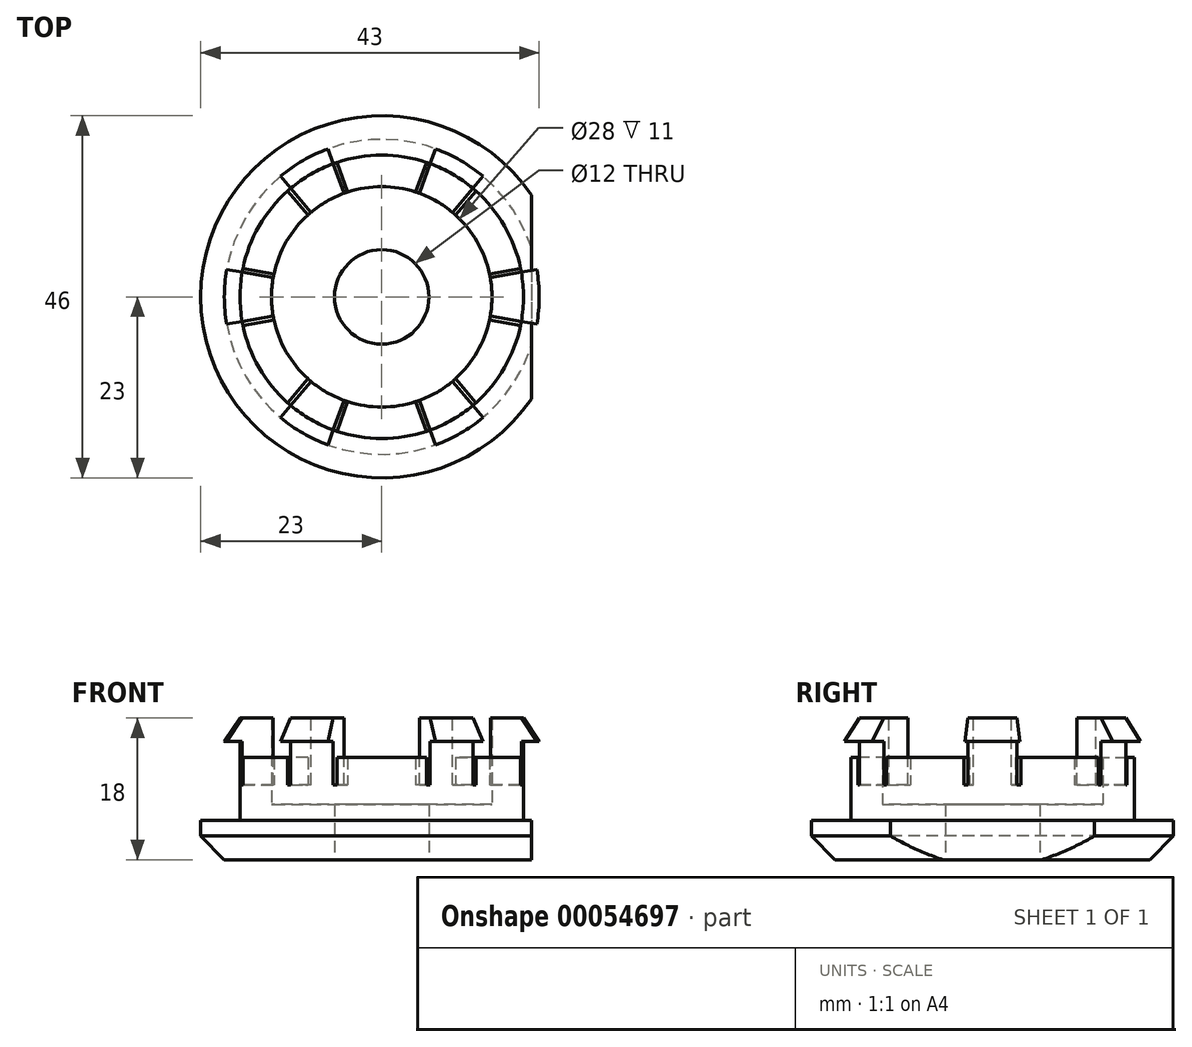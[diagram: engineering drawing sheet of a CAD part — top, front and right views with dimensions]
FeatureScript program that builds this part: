
annotation { "Feature Type Name" : "Feature", "Feature Type Description" : "" }
export const myFeature = defineFeature(function(context is Context, id is Id, definition is map)
    precondition{}
    {
        {
            var Q0;
            Q0=qCreatedBy(makeId("Top.planeOp"),FACE);
            var sketch = newSketch(context, id + "F0", { "sketchPlane" : qUnion([Q0])});
            skCircle(sketch, "E0", {"center": v(0, 0) * mm, "radius": 18 * mm});
            skCircle(sketch, "E1", {"center": v(0, 0) * mm, "radius": 6 * mm});
            skCircle(sketch, "E2", {"center": v(0, 0) * mm, "radius": 23 * mm});
            skCircle(sketch, "E3", {"center": v(0, 0) * mm, "radius": 14 * mm});
            skSolve(sketch);
        }
        {
            var Q0;
            Q0=makeQuery(id+"F0.imprint","IMPRINT",FACE,{"disambiguationData":[TD([[makeQuery(id+"F0.imprint","IMPRINT",EDGE,{"derivedFrom":sQuery(id+"F0.wireOp",EDGE,"E0")}),1.0]])]});
            var Q1;
            Q1=makeQuery(id+"F0.imprint","IMPRINT",FACE,{"disambiguationData":[TD([[makeQuery(id+"F0.imprint","IMPRINT",EDGE,{"derivedFrom":sQuery(id+"F0.wireOp",EDGE,"E1")}),-1.0]])]});
            extrude(context, id + "F1", {"entities" : qUnion([Q0, Q1]), "depth" : 2 * mm});
        }
        {
            var Q0;
            Q0=makeQuery(id+"F0.imprint","IMPRINT",FACE,{"disambiguationData":[TD([[makeQuery(id+"F0.imprint","IMPRINT",EDGE,{"derivedFrom":sQuery(id+"F0.wireOp",EDGE,"E0")}),1.0]])]});
            extrude(context, id + "F2", {"entities" : qUnion([Q0]), "operationType" : NewBodyOperationType.ADD, "depth" : 13 * mm});
        }
        {
            var Q0;
            Q0=makeQuery(id+"F0.imprint","IMPRINT",FACE,{"disambiguationData":[TD([[makeQuery(id+"F0.imprint","IMPRINT",EDGE,{"derivedFrom":sQuery(id+"F0.wireOp",EDGE,"E0")}),-1.0]])]});
            var Q1;
            Q1=makeQuery(id+"F0.imprint","IMPRINT",FACE,{"disambiguationData":[TD([[makeQuery(id+"F0.imprint","IMPRINT",EDGE,{"derivedFrom":sQuery(id+"F0.wireOp",EDGE,"E0")}),1.0]])]});
            var Q2;
            Q2=makeQuery(id+"F0.imprint","IMPRINT",FACE,{"disambiguationData":[TD([[makeQuery(id+"F0.imprint","IMPRINT",EDGE,{"derivedFrom":sQuery(id+"F0.wireOp",EDGE,"E1")}),-1.0]])]});
            extrude(context, id + "F3", {"entities" : qUnion([Q0, Q1, Q2]), "operationType" : NewBodyOperationType.ADD, "oppositeDirection" : true, "depth" : 5 * mm});
        }
        {
            var Q0;
            Q0=makeQuery(id+"F3.opExtrude","CAP_EDGE",EDGE,{"disambiguationData":[OSD([sQuery(id+"F0.wireOp",EDGE,"E2")])],"isStart":false});
            chamfer(context, id + "F4", {"entities" : qUnion([Q0]), "width" : 3 * mm, "tangentPropagation" : true});
        }
        {
            var Q0;
            Q0=qCreatedBy(makeId("Front.planeOp"),FACE);
            var sketch = newSketch(context, id + "F5", { "sketchPlane" : qUnion([Q0])});
            skLineSegment(sketch, "E4", {"start": v(14, 10) * mm, "end": v(14, 13) * mm});
            skLineSegment(sketch, "E5", {"start": v(14, 13) * mm, "end": v(18, 13) * mm});
            skLineSegment(sketch, "E6", {"start": v(18, 13) * mm, "end": v(20, 10) * mm});
            skLineSegment(sketch, "E7", {"start": v(20, 10) * mm, "end": v(14, 10) * mm});
            skLineSegment(sketch, "E8", {"start": v(0, 0) * mm, "end": v(0, 19.84) * mm});
            skLineSegment(sketch, "E9", {"start": v(18, 13) * mm, "end": v(18, 5) * mm});
            skLineSegment(sketch, "E10", {"start": v(18, 5) * mm, "end": v(14, 5) * mm});
            skLineSegment(sketch, "E11", {"start": v(14, 5) * mm, "end": v(14, 10) * mm});
            skSolve(sketch);
        }
        {
            var Q0;
            Q0=makeQuery(id+"F5.imprint","IMPRINT",FACE,{"disambiguationData":[TD([[makeQuery(id+"F5.imprint","IMPRINT",EDGE,{"derivedFrom":sQuery(id+"F5.wireOp",EDGE,"E4")}),-1.0]])]});
            var Q1;
            {var subQ0=sQuery(id+"F5.wireOp",EDGE,"E6");Q1=makeQuery(id+"F5.imprint","IMPRINT",FACE,{"disambiguationData":[TD([[makeQuery(id+"F5.imprint","IMPRINT",EDGE,{"derivedFrom":subQ0}),-1.0]])]});}
            var Q2;
            {var subQ4=sQuery(id+"F5.wireOp",EDGE,"E10");Q2=makeQuery(id+"F5.imprint","IMPRINT",FACE,{"disambiguationData":[TD([[makeQuery(id+"F5.imprint","IMPRINT",EDGE,{"derivedFrom":subQ4}),-1.0]])]});}
            var Q3;
            Q3=sQuery(id+"F5.wireOp",EDGE,"E8");
            revolve(context, id + "F6", {"entities" : qUnion([Q0, Q1, Q2]), "axis" : qUnion([Q3]), "revolveType" : RevolveType.SYMMETRIC, "angle" : 20 * degree});
        }
        {
            var Q0;
            Q0=makeQuery(id+"F6.opRevolve","SWEPT_BODY",BODY,{"disambiguationData":[OSD([sQuery(id+"F5.wireOp",EDGE,"E4"),sQuery(id+"F5.wireOp",EDGE,"E5"),sQuery(id+"F5.wireOp",EDGE,"E6"),sQuery(id+"F5.wireOp",EDGE,"E7")])]});
            var Q1;
            Q1=sQuery(id+"F5.wireOp",EDGE,"E8");
            circularPattern(context, id + "F7", {"entities" : qUnion([Q0]), "axis" : qUnion([Q1]), "angle" : 360 * degree, "instanceCount" : 6, "equalSpace" : true});
        }
        {
            var Q0;
            Q0=makeQuery(id+"F6.opRevolve","SWEPT_BODY",BODY,{"disambiguationData":[OSD([sQuery(id+"F5.wireOp",EDGE,"E4"),sQuery(id+"F5.wireOp",EDGE,"E5"),sQuery(id+"F5.wireOp",EDGE,"E6"),sQuery(id+"F5.wireOp",EDGE,"E7"),sQuery(id+"F5.wireOp",EDGE,"E9"),sQuery(id+"F5.wireOp",EDGE,"E10"),sQuery(id+"F5.wireOp",EDGE,"E11")])]});
            var Q1;
            Q1=makeQuery(id+"F7.opPattern","COPY",BODY,{"derivedFrom":makeQuery(id+"F6.opRevolve","SWEPT_BODY",BODY,{"disambiguationData":[OSD([sQuery(id+"F5.wireOp",EDGE,"E4"),sQuery(id+"F5.wireOp",EDGE,"E5"),sQuery(id+"F5.wireOp",EDGE,"E6"),sQuery(id+"F5.wireOp",EDGE,"E7"),sQuery(id+"F5.wireOp",EDGE,"E9"),sQuery(id+"F5.wireOp",EDGE,"E10"),sQuery(id+"F5.wireOp",EDGE,"E11")])]}),"instanceName":"1"});
            var Q2;
            Q2=makeQuery(id+"F7.opPattern","COPY",BODY,{"derivedFrom":makeQuery(id+"F6.opRevolve","SWEPT_BODY",BODY,{"disambiguationData":[OSD([sQuery(id+"F5.wireOp",EDGE,"E4"),sQuery(id+"F5.wireOp",EDGE,"E5"),sQuery(id+"F5.wireOp",EDGE,"E6"),sQuery(id+"F5.wireOp",EDGE,"E7"),sQuery(id+"F5.wireOp",EDGE,"E9"),sQuery(id+"F5.wireOp",EDGE,"E10"),sQuery(id+"F5.wireOp",EDGE,"E11")])]}),"instanceName":"2"});
            var Q3;
            Q3=makeQuery(id+"F7.opPattern","COPY",BODY,{"derivedFrom":makeQuery(id+"F6.opRevolve","SWEPT_BODY",BODY,{"disambiguationData":[OSD([sQuery(id+"F5.wireOp",EDGE,"E4"),sQuery(id+"F5.wireOp",EDGE,"E5"),sQuery(id+"F5.wireOp",EDGE,"E6"),sQuery(id+"F5.wireOp",EDGE,"E7"),sQuery(id+"F5.wireOp",EDGE,"E9"),sQuery(id+"F5.wireOp",EDGE,"E10"),sQuery(id+"F5.wireOp",EDGE,"E11")])]}),"instanceName":"3"});
            var Q4;
            Q4=makeQuery(id+"F7.opPattern","COPY",BODY,{"derivedFrom":makeQuery(id+"F6.opRevolve","SWEPT_BODY",BODY,{"disambiguationData":[OSD([sQuery(id+"F5.wireOp",EDGE,"E4"),sQuery(id+"F5.wireOp",EDGE,"E5"),sQuery(id+"F5.wireOp",EDGE,"E6"),sQuery(id+"F5.wireOp",EDGE,"E7"),sQuery(id+"F5.wireOp",EDGE,"E9"),sQuery(id+"F5.wireOp",EDGE,"E10"),sQuery(id+"F5.wireOp",EDGE,"E11")])]}),"instanceName":"4"});
            var Q5;
            Q5=makeQuery(id+"F7.opPattern","COPY",BODY,{"derivedFrom":makeQuery(id+"F6.opRevolve","SWEPT_BODY",BODY,{"disambiguationData":[OSD([sQuery(id+"F5.wireOp",EDGE,"E4"),sQuery(id+"F5.wireOp",EDGE,"E5"),sQuery(id+"F5.wireOp",EDGE,"E6"),sQuery(id+"F5.wireOp",EDGE,"E7"),sQuery(id+"F5.wireOp",EDGE,"E9"),sQuery(id+"F5.wireOp",EDGE,"E10"),sQuery(id+"F5.wireOp",EDGE,"E11")])]}),"instanceName":"5"});
            var Q6;
            Q6=makeQuery(id+"F1.opExtrude","SWEPT_BODY",BODY,{"disambiguationData":[OSD([sQuery(id+"F0.wireOp",EDGE,"E0"),sQuery(id+"F0.wireOp",EDGE,"E1")])]});
            booleanBodies(context, id + "F8", {"operationType" : BooleanOperationType.SUBTRACTION, "tools" : qUnion([Q0, Q1, Q2, Q3, Q4, Q5]), "targets" : qUnion([Q6]), "offset" : true, "offsetAll" : true, "offsetDistance" : 0.5 * mm, "keepTools" : true});
        }
        {
            var Q0;
            Q0=makeQuery(id+"F7.opPattern","COPY",FACE,{"derivedFrom":makeQuery(id+"F6.opRevolve","SWEPT_FACE",FACE,{"disambiguationData":[OSD([sQuery(id+"F5.wireOp",EDGE,"E10")])]}),"instanceName":"4"});
            var Q1;
            Q1=makeQuery(id+"F7.opPattern","COPY",FACE,{"derivedFrom":makeQuery(id+"F6.opRevolve","SWEPT_FACE",FACE,{"disambiguationData":[OSD([sQuery(id+"F5.wireOp",EDGE,"E10")])]}),"instanceName":"5"});
            var Q2;
            Q2=makeQuery(id+"F6.opRevolve","SWEPT_FACE",FACE,{"disambiguationData":[OSD([sQuery(id+"F5.wireOp",EDGE,"E10")])]});
            var Q3;
            Q3=makeQuery(id+"F7.opPattern","COPY",FACE,{"derivedFrom":makeQuery(id+"F6.opRevolve","SWEPT_FACE",FACE,{"disambiguationData":[OSD([sQuery(id+"F5.wireOp",EDGE,"E10")])]}),"instanceName":"1"});
            var Q4;
            Q4=makeQuery(id+"F7.opPattern","COPY",FACE,{"derivedFrom":makeQuery(id+"F6.opRevolve","SWEPT_FACE",FACE,{"disambiguationData":[OSD([sQuery(id+"F5.wireOp",EDGE,"E10")])]}),"instanceName":"2"});
            var Q5;
            Q5=makeQuery(id+"F7.opPattern","COPY",FACE,{"derivedFrom":makeQuery(id+"F6.opRevolve","SWEPT_FACE",FACE,{"disambiguationData":[OSD([sQuery(id+"F5.wireOp",EDGE,"E10")])]}),"instanceName":"3"});
            extrude(context, id + "F9", {"entities" : qUnion([Q0, Q1, Q2, Q3, Q4, Q5]), "operationType" : NewBodyOperationType.ADD, "depth" : 5 * mm});
        }
        {
            var Q0;
            {var subQ0=sQuery(id+"F5.wireOp",EDGE,"E11");var subQ1=sQuery(id+"F5.wireOp",EDGE,"E10");var subQ2=sQuery(id+"F5.wireOp",EDGE,"E9");var subQ3=sQuery(id+"F5.wireOp",EDGE,"E7");var subQ4=sQuery(id+"F5.wireOp",EDGE,"E6");var subQ5=sQuery(id+"F5.wireOp",EDGE,"E5");var subQ6=sQuery(id+"F5.wireOp",EDGE,"E4");var subQ7=sQuery(id+"F0.wireOp",EDGE,"E0");var subQ8=sQuery(id+"F0.wireOp",EDGE,"E3");Q0=makeQuery(id+"F8.tempBoolean.opBoolean","SPLIT",FACE,{"disambiguationData":[TD([makeQuery(id+"F8.offsetTempBody.opPattern","COPY",FACE,{"derivedFrom":makeQuery(id+"F7.opPattern","COPY",FACE,{"derivedFrom":makeQuery(id+"F6.opRevolve","CAP_FACE",FACE,{"disambiguationData":[OSD([subQ6,subQ5,subQ4,subQ3,subQ2,subQ1,subQ0])],"isStart":false}),"instanceName":"2"}),"instanceName":"1"})])],"derivedFrom":makeQuery(id+"F2.opExtrude","CAP_FACE",FACE,{"disambiguationData":[OSD([subQ7,subQ8])],"isStart":false})});}
            var Q1;
            {var subQ0=sQuery(id+"F0.wireOp",EDGE,"E3");var subQ1=sQuery(id+"F0.wireOp",EDGE,"E0");var subQ2=sQuery(id+"F5.wireOp",EDGE,"E11");var subQ3=sQuery(id+"F5.wireOp",EDGE,"E10");var subQ4=sQuery(id+"F5.wireOp",EDGE,"E9");var subQ5=sQuery(id+"F5.wireOp",EDGE,"E7");var subQ6=sQuery(id+"F5.wireOp",EDGE,"E6");var subQ7=sQuery(id+"F5.wireOp",EDGE,"E5");var subQ8=sQuery(id+"F5.wireOp",EDGE,"E4");Q1=makeQuery(id+"F8.tempBoolean.opBoolean","SPLIT",FACE,{"disambiguationData":[TD([makeQuery(id+"F8.offsetTempBody.opPattern","COPY",FACE,{"derivedFrom":makeQuery(id+"F7.opPattern","COPY",FACE,{"derivedFrom":makeQuery(id+"F6.opRevolve","CAP_FACE",FACE,{"disambiguationData":[OSD([subQ8,subQ7,subQ6,subQ5,subQ4,subQ3,subQ2])],"isStart":false}),"instanceName":"3"}),"instanceName":"1"})])],"derivedFrom":makeQuery(id+"F2.opExtrude","CAP_FACE",FACE,{"disambiguationData":[OSD([subQ1,subQ0])],"isStart":false})});}
            var Q2;
            {var subQ0=sQuery(id+"F5.wireOp",EDGE,"E11");var subQ1=sQuery(id+"F5.wireOp",EDGE,"E10");var subQ2=sQuery(id+"F5.wireOp",EDGE,"E9");var subQ3=sQuery(id+"F5.wireOp",EDGE,"E7");var subQ4=sQuery(id+"F5.wireOp",EDGE,"E6");var subQ5=sQuery(id+"F5.wireOp",EDGE,"E5");var subQ6=sQuery(id+"F5.wireOp",EDGE,"E4");var subQ7=sQuery(id+"F0.wireOp",EDGE,"E3");var subQ8=sQuery(id+"F0.wireOp",EDGE,"E0");Q2=makeQuery(id+"F8.tempBoolean.opBoolean","SPLIT",FACE,{"disambiguationData":[TD([makeQuery(id+"F8.offsetTempBody.opPattern","COPY",FACE,{"derivedFrom":makeQuery(id+"F7.opPattern","COPY",FACE,{"derivedFrom":makeQuery(id+"F6.opRevolve","CAP_FACE",FACE,{"disambiguationData":[OSD([subQ6,subQ5,subQ4,subQ3,subQ2,subQ1,subQ0])],"isStart":false}),"instanceName":"4"}),"instanceName":"1"})])],"derivedFrom":makeQuery(id+"F2.opExtrude","CAP_FACE",FACE,{"disambiguationData":[OSD([subQ8,subQ7])],"isStart":false})});}
            var Q3;
            {var subQ0=sQuery(id+"F0.wireOp",EDGE,"E3");var subQ1=sQuery(id+"F0.wireOp",EDGE,"E0");var subQ2=sQuery(id+"F5.wireOp",EDGE,"E11");var subQ3=sQuery(id+"F5.wireOp",EDGE,"E10");var subQ4=sQuery(id+"F5.wireOp",EDGE,"E9");var subQ5=sQuery(id+"F5.wireOp",EDGE,"E7");var subQ6=sQuery(id+"F5.wireOp",EDGE,"E6");var subQ7=sQuery(id+"F5.wireOp",EDGE,"E5");var subQ8=sQuery(id+"F5.wireOp",EDGE,"E4");Q3=makeQuery(id+"F8.tempBoolean.opBoolean","SPLIT",FACE,{"disambiguationData":[TD([makeQuery(id+"F8.offsetTempBody.opPattern","COPY",FACE,{"derivedFrom":makeQuery(id+"F6.opRevolve","CAP_FACE",FACE,{"disambiguationData":[OSD([subQ8,subQ7,subQ6,subQ5,subQ4,subQ3,subQ2])],"isStart":true}),"instanceName":"1"})])],"derivedFrom":makeQuery(id+"F2.opExtrude","CAP_FACE",FACE,{"disambiguationData":[OSD([subQ1,subQ0])],"isStart":false})});}
            var Q4;
            {var subQ0=sQuery(id+"F0.wireOp",EDGE,"E3");var subQ1=sQuery(id+"F5.wireOp",EDGE,"E11");var subQ2=sQuery(id+"F5.wireOp",EDGE,"E10");var subQ3=sQuery(id+"F5.wireOp",EDGE,"E9");var subQ4=sQuery(id+"F5.wireOp",EDGE,"E7");var subQ5=sQuery(id+"F5.wireOp",EDGE,"E6");var subQ6=sQuery(id+"F5.wireOp",EDGE,"E5");var subQ7=sQuery(id+"F5.wireOp",EDGE,"E4");var subQ8=sQuery(id+"F0.wireOp",EDGE,"E0");Q4=makeQuery(id+"F8.tempBoolean.opBoolean","SPLIT",FACE,{"disambiguationData":[TD([makeQuery(id+"F8.offsetTempBody.opPattern","COPY",FACE,{"derivedFrom":makeQuery(id+"F6.opRevolve","CAP_FACE",FACE,{"disambiguationData":[OSD([subQ7,subQ6,subQ5,subQ4,subQ3,subQ2,subQ1])],"isStart":false}),"instanceName":"1"})])],"derivedFrom":makeQuery(id+"F2.opExtrude","CAP_FACE",FACE,{"disambiguationData":[OSD([subQ8,subQ0])],"isStart":false})});}
            var Q5;
            {var subQ0=sQuery(id+"F5.wireOp",EDGE,"E11");var subQ1=sQuery(id+"F5.wireOp",EDGE,"E10");var subQ2=sQuery(id+"F5.wireOp",EDGE,"E9");var subQ3=sQuery(id+"F5.wireOp",EDGE,"E7");var subQ4=sQuery(id+"F5.wireOp",EDGE,"E6");var subQ5=sQuery(id+"F5.wireOp",EDGE,"E5");var subQ6=sQuery(id+"F5.wireOp",EDGE,"E4");var subQ7=sQuery(id+"F0.wireOp",EDGE,"E3");var subQ8=sQuery(id+"F0.wireOp",EDGE,"E0");Q5=makeQuery(id+"F8.tempBoolean.opBoolean","SPLIT",FACE,{"disambiguationData":[TD([makeQuery(id+"F8.offsetTempBody.opPattern","COPY",FACE,{"derivedFrom":makeQuery(id+"F7.opPattern","COPY",FACE,{"derivedFrom":makeQuery(id+"F6.opRevolve","CAP_FACE",FACE,{"disambiguationData":[OSD([subQ6,subQ5,subQ4,subQ3,subQ2,subQ1,subQ0])],"isStart":false}),"instanceName":"1"}),"instanceName":"1"})])],"derivedFrom":makeQuery(id+"F2.opExtrude","CAP_FACE",FACE,{"disambiguationData":[OSD([subQ8,subQ7])],"isStart":false})});}
            extrude(context, id + "F10", {"entities" : qUnion([Q0, Q1, Q2, Q3, Q4, Q5]), "operationType" : NewBodyOperationType.REMOVE, "oppositeDirection" : true, "depth" : 5 * mm});
        }
        {
            var Q0;
            Q0=makeQuery(id+"F0.imprint","IMPRINT",FACE,{"disambiguationData":[TD([[makeQuery(id+"F0.imprint","IMPRINT",EDGE,{"derivedFrom":sQuery(id+"F0.wireOp",EDGE,"E0")}),-1.0]])]});
            var sketch = newSketch(context, id + "F11", { "sketchPlane" : qUnion([Q0])});
            skLineSegment(sketch, "E12", {"start": v(19, 12.96) * mm, "end": v(19, -12.96) * mm});
            skSolve(sketch);
        }
        {
            var Q0;
            {var subQ0=sQuery(id+"F11.wireOp",EDGE,"E12");Q0=makeQuery(id+"F11.imprint","IMPRINT",FACE,{"disambiguationData":[TD([[makeQuery(id+"F11.imprint","IMPRINT",EDGE,{"derivedFrom":subQ0}),1.0]])]});}
            extrude(context, id + "F12", {"entities" : qUnion([Q0]), "operationType" : NewBodyOperationType.REMOVE, "oppositeDirection" : true, "depth" : 25 * mm});
        }
    });
